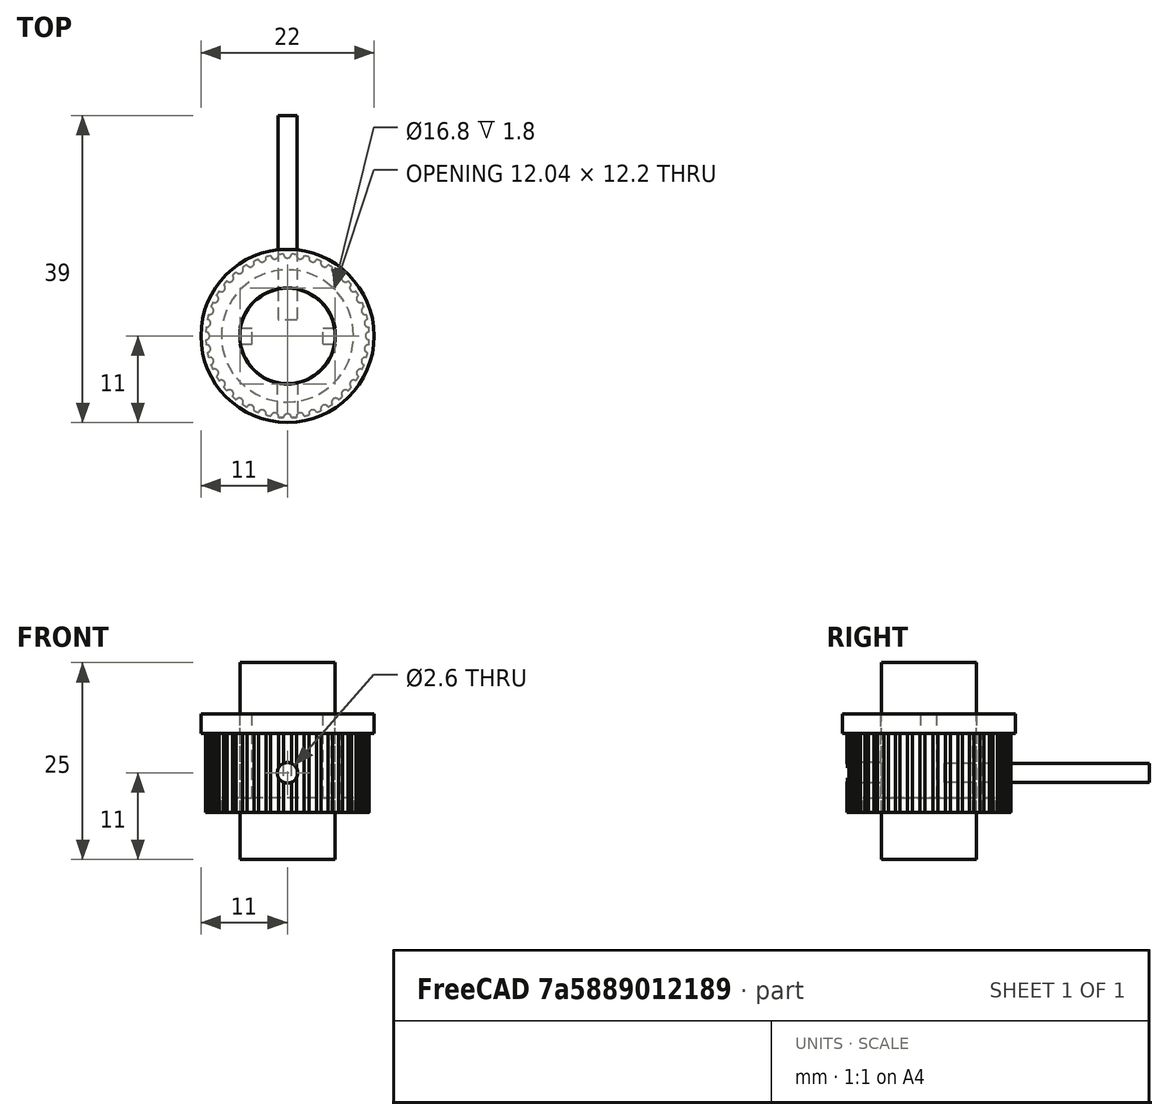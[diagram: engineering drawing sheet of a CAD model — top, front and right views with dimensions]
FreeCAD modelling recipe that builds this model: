
FCSTD DOCUMENT  (FreeCAD 0.17R13522 (Git))
Label: v5_perilla_grande
License: CreativeCommons Attribution-ShareAlike
LicenseURL: http://creativecommons.org/licenses/by-sa/4.0/
objects: Part::Cylinder×7, Part::Cut×7, Part::Feature×3, Part::Fuse×2, Part::Box×2, Part::FeaturePython×1
note: 22 computed .brp shape members not serialized (recipe doc carries the construction recipe); baked Part::Feature solids carry a one-line shape summary decoded from their .brp

FEATURE [Part::Cylinder] Cylinder
  Angle = 360
  AttacherType = Attacher::AttachEngine3D
  Height = 2.5
  Radius = 11
FEATURE [Part::Cylinder] Cylinder001  label="agujereador del medio"
  Angle = 360
  AttacherType = Attacher::AttachEngine3D
  Height = 25
  Placement = pos=(0,0,-16) rot=(0,0,1;0rad)
  Radius = 6.1
FEATURE [Part::Cut] Cut
  Base = -> Cylinder
  Refine = true
  Tool = -> Cylinder001
FEATURE [Part::Cylinder] Cylinder002
  Angle = 360
  AttacherType = Attacher::AttachEngine3D
  Height = 12.2
  Placement = pos=(0,0,-10) rot=(0,0,1;0rad)
  Radius = 10.4
FEATURE [Part::Feature] Cylinder001001  label="Cylinder003"
  Placement = pos=(0,0,-16) rot=(0,0,1;0rad)
  shape: bbox 12.1 x 12.1 x 25 mm, 3 faces (baked)
FEATURE [Part::Feature] Cylinder001002  label="Cylinder004"
  Placement = pos=(0,0,-16) rot=(0,0,1;0rad)
  shape: bbox 12.1 x 12.1 x 25 mm, 3 faces (baked)
FEATURE [Part::Cylinder] Cylinder001003  label="Cylinder005"
  Angle = 360
  AttacherType = Attacher::AttachEngine3D
  Height = 10
  Placement = pos=(0,0,-18.2) rot=(0,0,1;0rad)
  Radius = 8.4
FEATURE [Part::Fuse] Fusion
  Base = -> Cut
  Refine = true
  Tool = -> Cylinder002
FEATURE [Part::Cut] Cut001
  Base = -> Fusion
  Refine = true
  Tool = -> Cylinder001003
FEATURE [Part::Cut] Cut002
  Base = -> Cut001
  Refine = true
  Tool = -> Cylinder001
FEATURE [Part::Cylinder] Cylinder001004  label="cavador_base"
  Angle = 360
  AttacherType = Attacher::AttachEngine3D
  Height = 12
  Placement = pos=(-10.4,0,-12) rot=(0,0,1;0rad)
  Radius = 0.5
FEATURE [Part::FeaturePython] Array  # Draft array (typed FeaturePython)
  Angle = 360
  ArrayType = 1
  Axis = (0,0,1)
  Base = -> Cylinder001004
  Center = (0,0,0)
  Fuse = false
  IntervalAxis = (0,0,0)
  IntervalX = (1,0,0)
  IntervalY = (0,1,0)
  IntervalZ = (0,0,0)
  NumberPolar = 40
  NumberX = 0
  NumberY = 0
  NumberZ = 0
FEATURE [Part::Cut] Cut003  label="el boton sin agujero"
  Base = -> Cut002
  Refine = true
  Tool = -> Array
FEATURE [Part::Cylinder] Cylinder001005  label="barilla perfora alen"
  Angle = 360
  AttacherType = Attacher::AttachEngine3D
  Height = 26
  Placement = pos=(0,0,-5) rot=(1,0,0;1.5708rad)
  Radius = 1.2
FEATURE [Part::Feature] Cylinder001005001  label="barilla perfora alen001"
  Placement = pos=(0,28,-5) rot=(1,0,0;1.5708rad)
  shape: bbox 2.4 x 26 x 2.4 mm, 3 faces (baked)
FEATURE [Part::Cut] Cut004  label="perilla con un agujero para allen"
  Base = -> Cut003
  Refine = true
  Tool = -> Cylinder001005
FEATURE [Part::Cylinder] Cylinder001005002  label="barilla perfora alen 2.6 mm"
  Angle = 360
  AttacherType = Attacher::AttachEngine3D
  Height = 18
  Placement = pos=(0,0,-5) rot=(1,0,0;1.5708rad)
  Radius = 1.3
FEATURE [Part::Cut] Cut005  label="perilla grande"
  Base = -> Cut004
  Refine = true
  Tool = -> Cylinder001005002
FEATURE [Part::Box] Box  label="aleta grande entera"
  AttacherType = Attacher::AttachEngine3D
  Height = 10.7
  Length = 14
  Placement = pos=(-7,-1,-8.2) rot=(0,0,1;0rad)
  Width = 2
FEATURE [Part::Box] Box001  label="cortador aleta grande"
  AttacherType = Attacher::AttachEngine3D
  Height = 10.7
  Length = 9
  Placement = pos=(-4.5,-1,-8.2) rot=(0,0,1;0rad)
  Width = 2
FEATURE [Part::Fuse] Fusion001
  Base = -> Cut005
  Refine = true
  Tool = -> Box
FEATURE [Part::Cut] Cut006  label="perilla grande con aletas"
  Base = -> Fusion001
  Refine = true
  Tool = -> Box001
